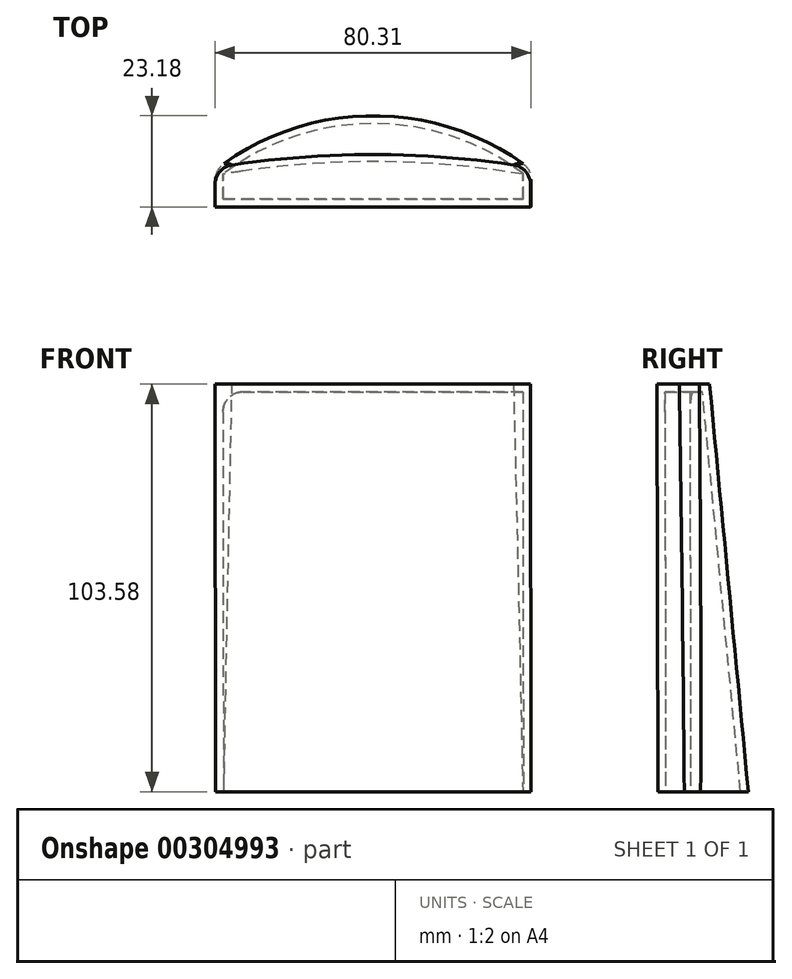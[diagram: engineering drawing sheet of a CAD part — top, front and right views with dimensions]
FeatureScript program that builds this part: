
annotation { "Feature Type Name" : "Feature", "Feature Type Description" : "" }
export const myFeature = defineFeature(function(context is Context, id is Id, definition is map)
    precondition{}
    {
        {
            var Q0;
            Q0=qCreatedBy(makeId("Top.planeOp"),FACE);
            var sketch = newSketch(context, id + "F0", { "sketchPlane" : qUnion([Q0])});
            skLineSegment(sketch, "E0", {"start": v(-37.95, -41.41) * mm, "end": v(38.25, -41.41) * mm});
            skLineSegment(sketch, "E1", {"start": v(-37.95, -41.41) * mm, "end": v(-37.95, -35.06) * mm});
            skLineSegment(sketch, "E2", {"start": v(38.25, -41.41) * mm, "end": v(38.25, -35.06) * mm});
            skArc(sketch, "E3", {"start": v(38.25, -35.06) * mm, "mid": v(0.15, -22.36) * mm, "end": v(-37.95, -35.06) * mm});
            skSolve(sketch);
        }
        {
            var Q0;
            Q0=qCreatedBy(makeId("Top.planeOp"),FACE);
            cPlane(context, id + "F1", {"entities" : qUnion([Q0]), "cplaneType" : CPlaneType.OFFSET, "offset" : 101.6 * mm, "width" : 152.4 * mm, "height" : 152.4 * mm});
        }
        {
            var Q0;
            Q0=qCreatedBy(id+"F1.planeOp",FACE);
            var sketch = newSketch(context, id + "F2", { "sketchPlane" : qUnion([Q0])});
            skLineSegment(sketch, "E4", {"start": v(-38.1, -41.57) * mm, "end": v(38.1, -41.57) * mm});
            skLineSegment(sketch, "E5", {"start": v(38.1, -41.57) * mm, "end": v(38.1, -35.22) * mm});
            skLineSegment(sketch, "E6", {"start": v(-38.1, -35.22) * mm, "end": v(-38.1, -41.57) * mm});
            skArc(sketch, "E7", {"start": v(38.1, -35.22) * mm, "mid": v(0, -32.04) * mm, "end": v(-38.1, -35.22) * mm});
            skSolve(sketch);
        }
        {
            var Q0;
            Q0=makeQuery(id+"F2.imprint","IMPRINT",FACE,{"disambiguationData":[TD([[makeQuery(id+"F2.imprint","IMPRINT",EDGE,{"derivedFrom":sQuery(id+"F2.wireOp",EDGE,"E4")}),1.0]])]});
            var Q1;
            Q1=makeQuery(id+"F0.imprint","IMPRINT",FACE,{"disambiguationData":[TD([[makeQuery(id+"F0.imprint","IMPRINT",EDGE,{"derivedFrom":sQuery(id+"F0.wireOp",EDGE,"E0")}),1.0]])]});
            loft(context, id + "F3", {"sheetProfilesArray" : [{ "sheetProfileEntities" : qUnion([Q0]) }, { "sheetProfileEntities" : qUnion([Q1]) }]});
        }
        {
            var Q0;
            Q0=makeQuery(id+"F3.opLoft","CAP_FACE",FACE,{"disambiguationData":[OSD([makeQuery(id+"F0.imprint","IMPRINT",FACE,{"disambiguationData":[TD([[makeQuery(id+"F0.imprint","IMPRINT",EDGE,{"derivedFrom":sQuery(id+"F0.wireOp",EDGE,"E0")}),1.0]])]})])],"isStart":true});
            shell(context, id + "F4", {"entities" : qUnion([Q0]), "thickness" : 1.98 * mm, "oppositeDirection" : true});
        }
        {
            var Q0;
            Q0=makeQuery(id+"F4.opShell","OFFSET_EDGE",EDGE,{"disambiguationData":[OSD([sQuery(id+"F2.wireOp",EDGE,"E4"),sQuery(id+"F2.wireOp",EDGE,"E6"),sQuery(id+"F2.wireOp",EDGE,"E7")])]});
            var Q1;
            Q1=makeQuery(id+"F3.opLoft","SWEPT_EDGE",EDGE,{"disambiguationData":[OSD([sQuery(id+"F0.wireOp",EDGE,"E2"),sQuery(id+"F0.wireOp",EDGE,"E3"),sQuery(id+"F2.wireOp",EDGE,"E5"),sQuery(id+"F2.wireOp",EDGE,"E7")])]});
            fillet(context, id + "F5", {"entities" : qUnion([Q0, Q1]), "radius" : 5.08 * mm, "tangentPropagation" : true, "allowEdgeOverflow" : false});
        }
        {
            var Q0;
            Q0=makeQuery(id+"F3.opLoft","SWEPT_EDGE",EDGE,{"disambiguationData":[OSD([sQuery(id+"F0.wireOp",EDGE,"E1"),sQuery(id+"F0.wireOp",EDGE,"E3"),sQuery(id+"F2.wireOp",EDGE,"E6"),sQuery(id+"F2.wireOp",EDGE,"E7")])]});
            fillet(context, id + "F6", {"entities" : qUnion([Q0]), "radius" : 5.08 * mm, "tangentPropagation" : true, "allowEdgeOverflow" : false});
        }
    });
